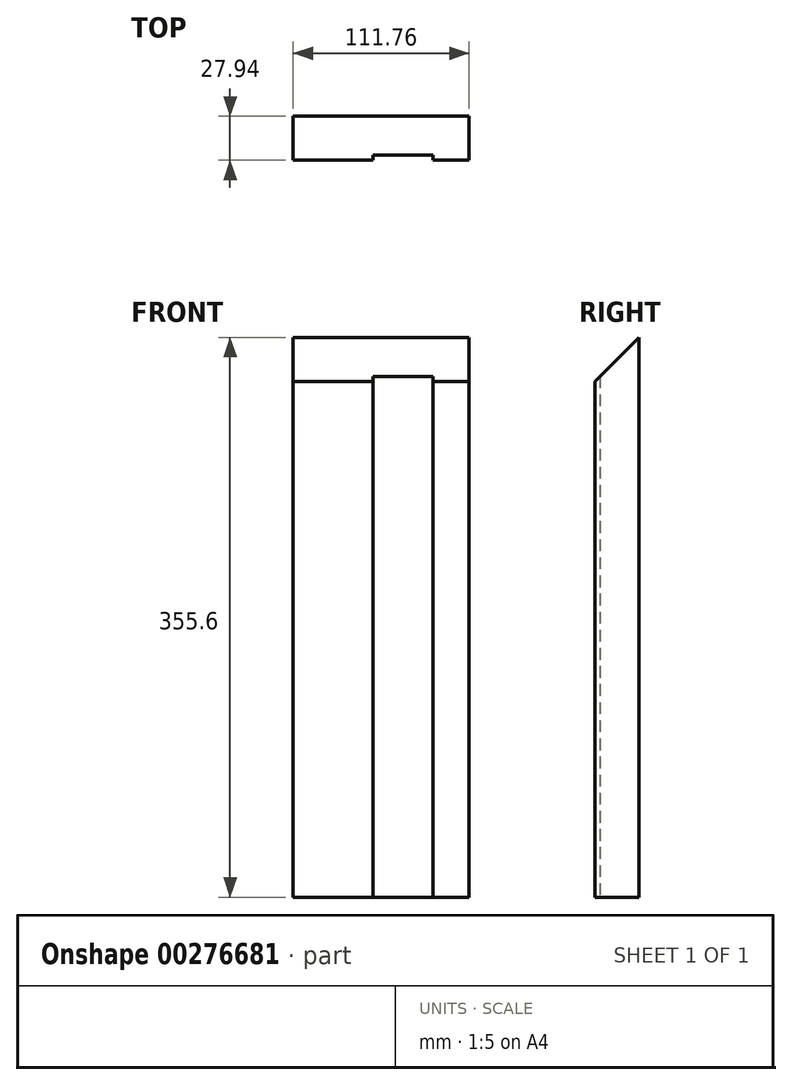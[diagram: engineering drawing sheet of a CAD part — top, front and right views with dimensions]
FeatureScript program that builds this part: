
annotation { "Feature Type Name" : "Feature", "Feature Type Description" : "" }
export const myFeature = defineFeature(function(context is Context, id is Id, definition is map)
    precondition{}
    {
        {
            var Q0;
            Q0=qCreatedBy(makeId("Top.planeOp"),FACE);
            var sketch = newSketch(context, id + "F0", { "sketchPlane" : qUnion([Q0])});
            skLineSegment(sketch, "E0.bottom", {"start": v(0, 0) * mm, "end": v(111.76, 0) * mm});
            skLineSegment(sketch, "E0.top", {"start": v(0, -27.94) * mm, "end": v(111.76, -27.94) * mm});
            skLineSegment(sketch, "E0.left", {"start": v(0, -27.94) * mm, "end": v(0, 0) * mm});
            skLineSegment(sketch, "E0.right", {"start": v(111.76, -27.94) * mm, "end": v(111.76, 0) * mm});
            skSolve(sketch);
        }
        {
            var Q0;
            Q0=qSketchRegion(id+"F0",true);
            extrude(context, id + "F1", {"entities" : qUnion([Q0]), "depth" : 355.6 * mm});
        }
        {
            var Q0;
            Q0=makeQuery(id+"F1.opExtrude","CAP_EDGE",EDGE,{"disambiguationData":[OSD([sQuery(id+"F0.wireOp",EDGE,"E0.top")])],"isStart":false});
            chamfer(context, id + "F2", {"entities" : qUnion([Q0]), "width" : 27.94 * mm, "tangentPropagation" : true});
        }
        {
            var Q0;
            Q0=makeQuery(id+"F1.opExtrude","SWEPT_FACE",FACE,{"disambiguationData":[OSD([sQuery(id+"F0.wireOp",EDGE,"E0.top")])]});
            var sketch = newSketch(context, id + "F3", { "sketchPlane" : qUnion([Q0])});
            skLineSegment(sketch, "E1.bottom", {"start": v(50.8, 355.6) * mm, "end": v(88.9, 355.6) * mm});
            skLineSegment(sketch, "E1.top", {"start": v(50.8, 0) * mm, "end": v(88.9, 0) * mm});
            skLineSegment(sketch, "E1.left", {"start": v(50.8, 355.6) * mm, "end": v(50.8, 0) * mm});
            skLineSegment(sketch, "E1.right", {"start": v(88.9, 355.6) * mm, "end": v(88.9, 0) * mm});
            skSolve(sketch);
        }
        {
            var Q0;
            {var subQ0=sQuery(id+"F3.wireOp",EDGE,"E1.bottom");Q0=makeQuery(id+"F3.imprint","IMPRINT",FACE,{"disambiguationData":[TD([[makeQuery(id+"F3.imprint","IMPRINT",EDGE,{"derivedFrom":subQ0}),-1.0]])]});}
            var Q1;
            {var subQ0=sQuery(id+"F3.wireOp",EDGE,"E1.top");Q1=makeQuery(id+"F3.imprint","IMPRINT",FACE,{"disambiguationData":[TD([[makeQuery(id+"F3.imprint","IMPRINT",EDGE,{"derivedFrom":subQ0}),1.0]])]});}
            extrude(context, id + "F4", {"entities" : qUnion([Q0, Q1]), "operationType" : NewBodyOperationType.REMOVE, "oppositeDirection" : true, "depth" : 3.17 * mm});
        }
    });
